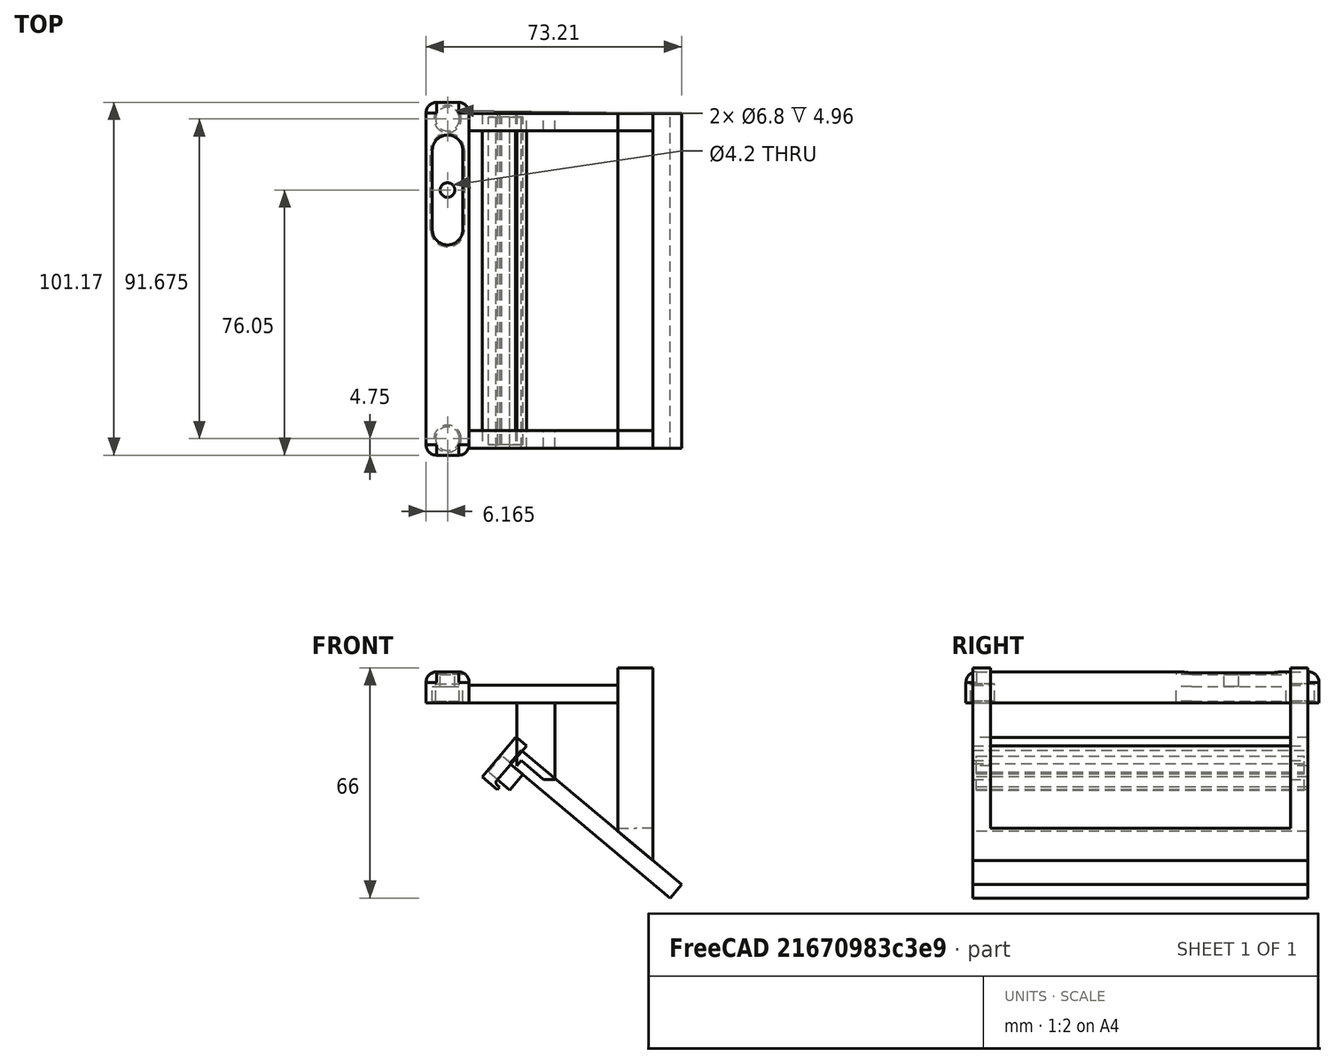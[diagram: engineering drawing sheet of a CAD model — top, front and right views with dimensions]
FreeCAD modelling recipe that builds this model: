
FCSTD DOCUMENT  (FreeCAD 1.0R39109 (Git))
Label: launch-stand
License: All rights reserved
LicenseURL: https://en.wikipedia.org/wiki/All_rights_reserved
objects: Part::Box×21, Part::Cut×11, Part::MultiFuse×2, Part::Feature×1, Part::Fillet×1, Mesh::Feature×1
note: 36 computed .brp shape members not serialized (recipe doc carries the construction recipe); baked Part::Feature solids carry a one-line shape summary decoded from their .brp

FEATURE [Part::Feature] Part__Feature  label="PN-000336 v7"
  shape: bbox 12.33 x 101.2 x 8.862 mm, 40 faces (baked)
FEATURE [Part::Box] Box  label="Cube"
  AttacherType = Attacher::AttachEngine3D
  Height = 5
  Length = 42.75
  Placement = pos=(12.25,2,0) rot=(0,0,1;0rad)
  Width = 5
FEATURE [Part::Box] Box001  label="Cube001"
  AttacherType = Attacher::AttachEngine3D
  Height = 5
  Length = 42.75
  Placement = pos=(12.25,93,0) rot=(0,0,1;0rad)
  Width = 5
FEATURE [Part::Box] Box003  label="Cube003"
  AttacherType = Attacher::AttachEngine3D
  Height = 49
  Length = 10
  Placement = pos=(40,2,-39) rot=(0,0,1;0rad)
  Width = 96
FEATURE [Part::Box] Box004  label="Cube004"
  AttacherType = Attacher::AttachEngine3D
  Height = 60
  Length = 5
  Placement = pos=(70,2,-56) rot=(0,1,0;-0.872665rad)
  Width = 96
FEATURE [Part::Box] Box005  label="Cube005"
  AttacherType = Attacher::AttachEngine3D
  Height = 49
  Length = 5
  Placement = pos=(45,7,-39) rot=(0,0,1;0rad)
  Width = 86
FEATURE [Part::Cut] Cut
  Base = -> Box003
  Tool = -> Box005
FEATURE [Part::Box] Box006  label="Cube006"
  AttacherType = Attacher::AttachEngine3D
  Height = 20
  Length = 10
  Placement = pos=(40,7,-10) rot=(0,0,1;0rad)
  Width = 86
FEATURE [Part::Cut] Cut001
  Base = -> Cut
  Tool = -> Box006
FEATURE [Part::Box] Box007  label="Cube007"
  AttacherType = Attacher::AttachEngine3D
  Height = 10
  Length = 10
  Placement = pos=(55,2,-46) rot=(0,0,1;0rad)
  Width = 96
FEATURE [Part::Box] Box008  label="Cube008"
  AttacherType = Attacher::AttachEngine3D
  Height = 10
  Length = 15
  Placement = pos=(13,2,-21) rot=(0,0,1;0rad)
  Width = 96
FEATURE [Part::Box] Box009  label="Cube009"
  AttacherType = Attacher::AttachEngine3D
  Height = 5
  Length = 14
  Placement = pos=(14,2,-21) rot=(0,0,1;0rad)
  Width = 96
FEATURE [Part::Cut] Cut002
  Base = -> Box008
  Tool = -> Box009
FEATURE [Part::Fillet] Fillet
  Base = -> Cut002
  EdgeLinks = -> Cut002 [Edge17]
  Edges = 1 edges r=1: [Edge17]
  Placement = pos=(-1.63,0,-23.03) rot=(0,1,0;5.42797rad)
FEATURE [Part::Box] Box011  label="Cube011"
  AttacherType = Attacher::AttachEngine3D
  Height = 24
  Length = 5
  Placement = pos=(40,7,-34) rot=(0,0,1;0rad)
  Width = 86
FEATURE [Part::Cut] Cut004
  Base = -> Cut001
  Placement = pos=(15,0,0) rot=(0,0,1;0rad)
  Tool = -> Box011
FEATURE [Part::Box] Box013  label="Cube013"
  AttacherType = Attacher::AttachEngine3D
  Height = 8
  Length = 6
  Placement = pos=(24,3,-25) rot=(0,0.1,0;-0.872665rad)
  Width = 94
FEATURE [Part::Box] Box014  label="Cube014"
  AttacherType = Attacher::AttachEngine3D
  Height = 2
  Length = 5
  Placement = pos=(55,7,-36) rot=(0,0,1;0rad)
  Width = 86
FEATURE [Part::Cut] Cut007
  Base = -> Cut004
  Tool = -> Box014
FEATURE [Part::MultiFuse] Fusion
  Shapes = -> [Box007,Cut007]
FEATURE [Part::Box] Box015  label="Cube015"
  AttacherType = Attacher::AttachEngine3D
  Height = 60
  Length = 5
  Placement = pos=(70,2,-59) rot=(0,1,0;-0.872665rad)
  Width = 96
FEATURE [Part::Cut] Cut008
  Base = -> Fusion
  Tool = -> Box015
FEATURE [Part::Box] Box016  label="Cube016"
  AttacherType = Attacher::AttachEngine3D
  Height = 60
  Length = 5
  Placement = pos=(70,2,-56) rot=(0,1,0;-0.872665rad)
  Width = 96
FEATURE [Part::Cut] Cut009
  Base = -> Cut008
  Tool = -> Box016
FEATURE [Part::Box] Box017  label="Cube017"
  AttacherType = Attacher::AttachEngine3D
  Height = 22
  Length = 11
  Placement = pos=(26,2,-22) rot=(0,0,1;0rad)
  Width = 5
FEATURE [Part::Box] Box018  label="Cube018"
  AttacherType = Attacher::AttachEngine3D
  Height = 22
  Length = 11
  Placement = pos=(26,93,-22) rot=(0,0,1;0rad)
  Width = 5
FEATURE [Part::Box] Box019  label="Cube019"
  AttacherType = Attacher::AttachEngine3D
  Height = 60
  Length = 5
  Placement = pos=(70,2,-59) rot=(0,1,0;-0.872665rad)
  Width = 96
FEATURE [Part::Box] Box020  label="Cube020"
  AttacherType = Attacher::AttachEngine3D
  Height = 60
  Length = 5
  Placement = pos=(70,2,-59) rot=(0,1,0;-0.872665rad)
  Width = 96
FEATURE [Part::Cut] Cut010
  Base = -> Box018
  Tool = -> Box019
FEATURE [Part::Cut] Cut011
  Base = -> Box017
  Tool = -> Box020
FEATURE [Mesh::Feature] control_v0_6  label="control-v0.6"
  Placement = pos=(17,-14.2033,-15.9974) rot=(0.684791,0.684791,-0.249244;3.63013rad)
FEATURE [Part::Box] Box021  label="Cube021"
  AttacherType = Attacher::AttachEngine3D
  Height = 10
  Length = 10
  Placement = pos=(25,1,-35) rot=(0,0.1,0;-0.872665rad)
  Width = 100
FEATURE [Part::Box] Box022  label="Cube022"
  AttacherType = Attacher::AttachEngine3D
  Height = 3
  Length = 16
  Placement = pos=(15.5,0,-22) rot=(0,0.1,0;-0.872665rad)
  Width = 102
FEATURE [Part::Box] Box023  label="Cube023"
  AttacherType = Attacher::AttachEngine3D
  Height = 2
  Length = 3
  Placement = pos=(25.98,0,-9.95) rot=(0,0.1,0;-1.5708rad)
  Width = 102
FEATURE [Part::MultiFuse] Fusion001
  Shapes = -> [Box023,Box022]
FEATURE [Part::Cut] Cut012
  Base = -> Fillet
  Tool = -> Fusion001
FEATURE [Part::Cut] Cut013
  Base = -> Cut012
  Tool = -> Box021
